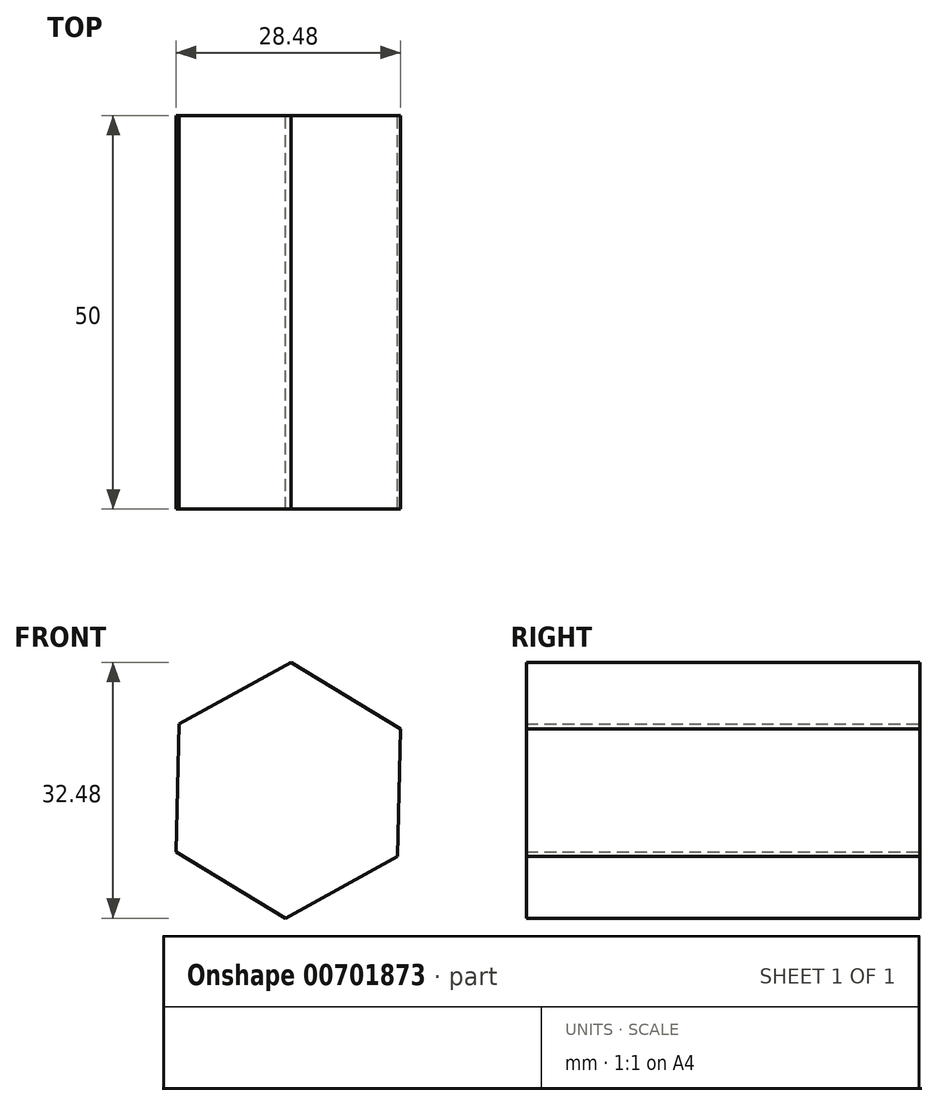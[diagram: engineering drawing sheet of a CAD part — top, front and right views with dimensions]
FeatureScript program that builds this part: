
annotation { "Feature Type Name" : "Feature", "Feature Type Description" : "" }
export const myFeature = defineFeature(function(context is Context, id is Id, definition is map)
    precondition{}
    {
        {
            var Q0;
            Q0=qCreatedBy(makeId("Front.planeOp"),FACE);
            var sketch = newSketch(context, id + "F0", { "sketchPlane" : qUnion([Q0])});
            skCircle(sketch, "E0.cCircle", {"center": v(0, 0) * mm, "radius": 16.24 * mm, "construction": true});
            skLineSegment(sketch, "E0.0", {"start": v(13.9, -8.42) * mm, "end": v(-0.35, -16.24) * mm});
            skLineSegment(sketch, "E0.1", {"start": v(-0.35, -16.24) * mm, "end": v(-14.24, -7.82) * mm});
            skLineSegment(sketch, "E0.2", {"start": v(-14.24, -7.82) * mm, "end": v(-13.9, 8.42) * mm});
            skLineSegment(sketch, "E0.3", {"start": v(-13.9, 8.42) * mm, "end": v(0.35, 16.24) * mm});
            skLineSegment(sketch, "E0.4", {"start": v(0.35, 16.24) * mm, "end": v(14.24, 7.82) * mm});
            skLineSegment(sketch, "E0.5", {"start": v(14.24, 7.82) * mm, "end": v(13.9, -8.42) * mm});
            skSolve(sketch);
        }
        {
            var Q0;
            Q0=makeQuery(id+"F0.imprint","IMPRINT",FACE,{"disambiguationData":[TD([[makeQuery(id+"F0.imprint","IMPRINT",EDGE,{"derivedFrom":sQuery(id+"F0.wireOp",EDGE,"E0.0")}),-1.0]])]});
            extrude(context, id + "F1", {"entities" : qUnion([Q0]), "depth" : 50 * mm, "offsetDistance" : 25 * mm});
        }
    });
